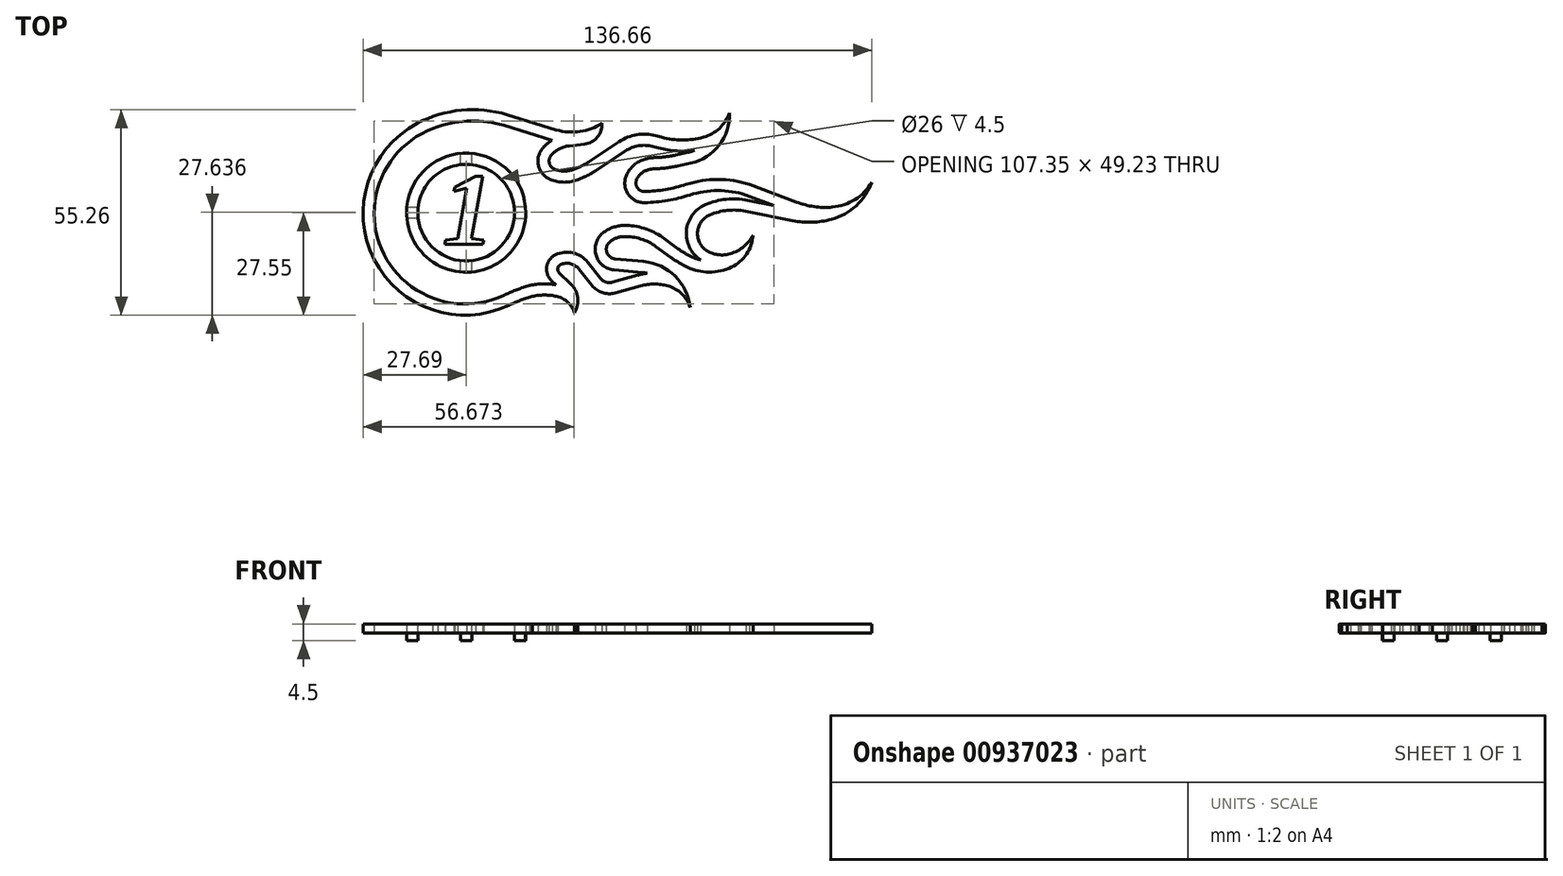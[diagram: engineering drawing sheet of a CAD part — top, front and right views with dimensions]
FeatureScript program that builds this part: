
annotation { "Feature Type Name" : "Feature", "Feature Type Description" : "" }
export const myFeature = defineFeature(function(context is Context, id is Id, definition is map)
    precondition{}
    {
        {
            var Q0;
            Q0=qCreatedBy(makeId("Top.planeOp"),FACE);
            cPlane(context, id + "F0", {"entities" : qUnion([Q0]), "cplaneType" : CPlaneType.OFFSET, "offset" : 2 * mm, "width" : 150 * mm, "height" : 150 * mm});
        }
        {
            var Q0;
            Q0=qCreatedBy(id+"F0.planeOp",FACE);
            var sketch = newSketch(context, id + "F1", { "sketchPlane" : qUnion([Q0])});
            skArc(sketch, "E0", {"start": v(-15.8, 20.8) * mm, "mid": v(-9.44, 20.3) * mm, "end": v(-3.49, 22.58) * mm});
            skLineSegment(sketch, "E1", {"start": v(-29, 24.82) * mm, "end": v(-15.8, 20.8) * mm});
            skArc(sketch, "E2", {"start": v(-53.14, 22.5) * mm, "mid": v(-64.76, -14.01) * mm, "end": v(-28.48, -26.36) * mm});
            skArc(sketch, "E3", {"start": v(-29, 24.82) * mm, "mid": v(-41.3, 26.06) * mm, "end": v(-53.14, 22.5) * mm});
            skArc(sketch, "E4", {"start": v(-8.25, 16.94) * mm, "mid": v(-4.75, 18.81) * mm, "end": v(-3.49, 22.58) * mm});
            skArc(sketch, "E5", {"start": v(-10.87, -28.44) * mm, "mid": v(-12.7, -25.58) * mm, "end": v(-15.7, -24) * mm});
            skArc(sketch, "E6", {"start": v(-15.7, -24) * mm, "mid": v(-18.94, -23.64) * mm, "end": v(-22.18, -24) * mm});
            skArc(sketch, "E7", {"start": v(-22.18, -24) * mm, "mid": v(-25.39, -25.04) * mm, "end": v(-28.48, -26.36) * mm});
            skArc(sketch, "E8", {"start": v(-10.87, -28.44) * mm, "mid": v(-10.04, -24.35) * mm, "end": v(-11.9, -20.62) * mm});
            skArc(sketch, "E9", {"start": v(-14.69, -15.51) * mm, "mid": v(-15.4, -16.45) * mm, "end": v(-15.02, -17.57) * mm});
            skLineSegment(sketch, "E10", {"start": v(-11.9, -20.62) * mm, "end": v(-15.02, -17.57) * mm});
            skArc(sketch, "E11", {"start": v(-9.7, -16.65) * mm, "mid": v(-12, -15.2) * mm, "end": v(-14.69, -15.51) * mm});
            skLineSegment(sketch, "E12", {"start": v(-9.7, -16.65) * mm, "end": v(-6.22, -21.05) * mm});
            skArc(sketch, "E13", {"start": v(-6.22, -21.05) * mm, "mid": v(-3.42, -23) * mm, "end": v(0, -23.09) * mm});
            skLineSegment(sketch, "E14", {"start": v(-8.25, 16.94) * mm, "end": v(-12.34, 16.47) * mm});
            skArc(sketch, "E15", {"start": v(-12.34, 16.47) * mm, "mid": v(-14.96, 15.66) * mm, "end": v(-17.12, 13.97) * mm});
            skArc(sketch, "E16", {"start": v(-17.12, 13.97) * mm, "mid": v(-17.66, 11.88) * mm, "end": v(-16.27, 10.22) * mm});
            skArc(sketch, "E17", {"start": v(-16.27, 10.22) * mm, "mid": v(-13.63, 9.69) * mm, "end": v(-10.98, 10.22) * mm});
            skLineSegment(sketch, "E18", {"start": v(-10.98, 10.22) * mm, "end": v(-9.42, 10.88) * mm});
            skLineSegment(sketch, "E19", {"start": v(1.1, 17.58) * mm, "end": v(-6.91, 12.23) * mm});
            skArc(sketch, "E20.filletArc", {"start": v(-9.42, 10.88) * mm, "mid": v(-8.13, 11.5) * mm, "end": v(-6.91, 12.23) * mm});
            skArc(sketch, "E21", {"start": v(10.9, 19.2) * mm, "mid": v(5.82, 19.45) * mm, "end": v(1.1, 17.58) * mm});
            skLineSegment(sketch, "E22", {"start": v(10.9, 19.2) * mm, "end": v(12.5, 18.78) * mm});
            skArc(sketch, "E23", {"start": v(12.5, 18.78) * mm, "mid": v(18.13, 18.04) * mm, "end": v(23.76, 18.78) * mm});
            skArc(sketch, "E24", {"start": v(23.76, 18.78) * mm, "mid": v(28.06, 21.17) * mm, "end": v(30.72, 25.31) * mm});
            skArc(sketch, "E25", {"start": v(20.3, 11.8) * mm, "mid": v(27.98, 16.65) * mm, "end": v(30.72, 25.31) * mm});
            skLineSegment(sketch, "E26", {"start": v(20.3, 11.8) * mm, "end": v(16.86, 11.06) * mm});
            skArc(sketch, "E27", {"start": v(10.82, 10.32) * mm, "mid": v(13.86, 10.55) * mm, "end": v(16.86, 11.06) * mm});
            skArc(sketch, "E28", {"start": v(10.82, 10.32) * mm, "mid": v(9.84, 10.23) * mm, "end": v(8.87, 10.03) * mm});
            skArc(sketch, "E29", {"start": v(8.87, 10.03) * mm, "mid": v(7.03, 9.04) * mm, "end": v(5.8, 7.34) * mm});
            skArc(sketch, "E30", {"start": v(5.8, 7.34) * mm, "mid": v(6.02, 5.16) * mm, "end": v(7.97, 4.17) * mm});
            skArc(sketch, "E31", {"start": v(19.12, 6.1) * mm, "mid": v(13.61, 4.74) * mm, "end": v(7.97, 4.17) * mm});
            skArc(sketch, "E32", {"start": v(36.14, 6.1) * mm, "mid": v(27.63, 7.44) * mm, "end": v(19.12, 6.1) * mm});
            skLineSegment(sketch, "E33", {"start": v(0, -23.09) * mm, "end": v(6.9, -21.19) * mm});
            skArc(sketch, "E34", {"start": v(14.19, -21.19) * mm, "mid": v(10.54, -20.7) * mm, "end": v(6.9, -21.19) * mm});
            skArc(sketch, "E35", {"start": v(20.17, -27.02) * mm, "mid": v(17.93, -23.33) * mm, "end": v(14.19, -21.19) * mm});
            skArc(sketch, "E36", {"start": v(20.17, -27.02) * mm, "mid": v(16.15, -18.57) * mm, "end": v(7.68, -14.62) * mm});
            skLineSegment(sketch, "E37", {"start": v(7.68, -14.62) * mm, "end": v(0, -13.91) * mm});
            skArc(sketch, "E38", {"start": v(-1.39, -9.32) * mm, "mid": v(-2.24, -12.08) * mm, "end": v(0, -13.91) * mm});
            skArc(sketch, "E39", {"start": v(2.46, -7.92) * mm, "mid": v(0.42, -8.3) * mm, "end": v(-1.39, -9.32) * mm});
            skArc(sketch, "E40", {"start": v(10.98, -10.59) * mm, "mid": v(6.94, -8.56) * mm, "end": v(2.46, -7.92) * mm});
            skLineSegment(sketch, "E41", {"start": v(10.98, -10.59) * mm, "end": v(15.06, -13.54) * mm});
            skArc(sketch, "E42", {"start": v(15.06, -13.54) * mm, "mid": v(17.16, -14.93) * mm, "end": v(19.37, -16.1) * mm});
            skArc(sketch, "E43", {"start": v(19.37, -16.1) * mm, "mid": v(25.34, -17.46) * mm, "end": v(31.3, -16.1) * mm});
            skArc(sketch, "E44", {"start": v(31.3, -16.1) * mm, "mid": v(35.34, -12.64) * mm, "end": v(37.05, -7.6) * mm});
            skArc(sketch, "E45", {"start": v(30.4, -12.7) * mm, "mid": v(34.29, -10.88) * mm, "end": v(37.05, -7.6) * mm});
            skArc(sketch, "E46", {"start": v(24.84, -11.81) * mm, "mid": v(27.53, -12.78) * mm, "end": v(30.4, -12.7) * mm});
            skArc(sketch, "E47", {"start": v(25.48, -2.1) * mm, "mid": v(22.17, -6.76) * mm, "end": v(24.84, -11.81) * mm});
            skArc(sketch, "E48", {"start": v(35.02, -1.1) * mm, "mid": v(30.17, -0.88) * mm, "end": v(25.48, -2.1) * mm});
            skLineSegment(sketch, "E49", {"start": v(35.02, -1.1) * mm, "end": v(47.7, -3.63) * mm});
            skArc(sketch, "E50", {"start": v(47.7, -3.63) * mm, "mid": v(52.94, -4.06) * mm, "end": v(58.13, -3.3) * mm});
            skArc(sketch, "E51", {"start": v(58.13, -3.3) * mm, "mid": v(64.79, 0.34) * mm, "end": v(68.97, 6.67) * mm});
            skArc(sketch, "E52", {"start": v(58.36, 0) * mm, "mid": v(64.48, 2.05) * mm, "end": v(68.97, 6.67) * mm});
            skArc(sketch, "E53", {"start": v(48.76, 1.34) * mm, "mid": v(53.49, 0.13) * mm, "end": v(58.36, 0) * mm});
            skLineSegment(sketch, "E54", {"start": v(36.14, 6.1) * mm, "end": v(48.76, 1.34) * mm});
            skArc(sketch, "E55.0", {"start": v(-29.87, 21.95) * mm, "mid": v(-38.73, 23.2) * mm, "end": v(-47.54, 21.67) * mm});
            skArc(sketch, "E56", {"start": v(-48.94, 21.12) * mm, "mid": v(-62.73, -11.25) * mm, "end": v(-29.8, -23.67) * mm});
            skLineSegment(sketch, "E57", {"start": v(-48.94, 21.12) * mm, "end": v(-47.54, 21.67) * mm});
            skLineSegment(sketch, "E58.0", {"start": v(-29.87, 21.95) * mm, "end": v(-16.92, 18) * mm});
            skArc(sketch, "E59.0", {"start": v(-12.68, 19.45) * mm, "mid": v(-12.7, 19.44) * mm, "end": v(-12.72, 19.44) * mm});
            skLineSegment(sketch, "E60", {"start": v(-16.92, 18) * mm, "end": v(-16.92, 18) * mm});
            skArc(sketch, "E61", {"start": v(-16.92, 18) * mm, "mid": v(-18.2, 17.08) * mm, "end": v(-19.34, 15.99) * mm});
            skArc(sketch, "E62.0", {"start": v(-19.37, 15.96) * mm, "mid": v(-20.58, 11.21) * mm, "end": v(-17.43, 7.46) * mm});
            skArc(sketch, "E63.0", {"start": v(-17.43, 7.46) * mm, "mid": v(-13.63, 6.69) * mm, "end": v(-9.82, 7.46) * mm});
            skLineSegment(sketch, "E64.0", {"start": v(-9.82, 7.46) * mm, "end": v(-8.25, 8.12) * mm});
            skArc(sketch, "E65.0", {"start": v(-8.25, 8.12) * mm, "mid": v(-6.71, 8.86) * mm, "end": v(-5.25, 9.74) * mm});
            skLineSegment(sketch, "E66.0", {"start": v(2.76, 15.09) * mm, "end": v(-5.25, 9.74) * mm});
            skArc(sketch, "E67.0", {"start": v(10.13, 16.3) * mm, "mid": v(6.31, 16.5) * mm, "end": v(2.76, 15.09) * mm});
            skLineSegment(sketch, "E68.0", {"start": v(10.13, 16.3) * mm, "end": v(11.74, 15.88) * mm});
            skArc(sketch, "E69.0", {"start": v(11.74, 15.88) * mm, "mid": v(16.51, 15.1) * mm, "end": v(21.35, 15.25) * mm});
            skLineSegment(sketch, "E70.0", {"start": v(19.3, 14.65) * mm, "end": v(16.22, 13.99) * mm});
            skArc(sketch, "E71.0", {"start": v(19.66, 14.73) * mm, "mid": v(20.52, 14.95) * mm, "end": v(21.35, 15.25) * mm});
            skArc(sketch, "E72.0", {"start": v(10.73, 13.32) * mm, "mid": v(13.5, 13.53) * mm, "end": v(16.22, 13.99) * mm});
            skArc(sketch, "E73.0", {"start": v(10.73, 13.32) * mm, "mid": v(9.4, 13.2) * mm, "end": v(8.08, 12.92) * mm});
            skArc(sketch, "E74.0", {"start": v(8.08, 12.92) * mm, "mid": v(5.05, 11.3) * mm, "end": v(3.04, 8.52) * mm});
            skArc(sketch, "E75.0", {"start": v(3.04, 8.52) * mm, "mid": v(3.54, 3.47) * mm, "end": v(8.07, 1.17) * mm});
            skArc(sketch, "E76.0", {"start": v(20.04, 3.25) * mm, "mid": v(14.12, 1.79) * mm, "end": v(8.07, 1.17) * mm});
            skLineSegment(sketch, "E77.0", {"start": v(35.6, 1.84) * mm, "end": v(42.66, 0.43) * mm});
            skArc(sketch, "E78.0", {"start": v(35.6, 1.84) * mm, "mid": v(29.87, 2.1) * mm, "end": v(24.3, 0.67) * mm});
            skArc(sketch, "E79.0", {"start": v(24.3, 0.67) * mm, "mid": v(19.19, -6.38) * mm, "end": v(23, -14.2) * mm});
            skArc(sketch, "E80.0", {"start": v(20.66, -13.4) * mm, "mid": v(21.81, -13.87) * mm, "end": v(23, -14.2) * mm});
            skArc(sketch, "E81.0", {"start": v(16.82, -11.12) * mm, "mid": v(18.69, -12.35) * mm, "end": v(20.66, -13.4) * mm});
            skLineSegment(sketch, "E82.0", {"start": v(12.74, -8.16) * mm, "end": v(16.82, -11.12) * mm});
            skArc(sketch, "E83.0", {"start": v(12.74, -8.16) * mm, "mid": v(7.83, -5.7) * mm, "end": v(2.4, -4.92) * mm});
            skArc(sketch, "E84.0", {"start": v(2.4, -4.92) * mm, "mid": v(-0.61, -5.48) * mm, "end": v(-3.28, -7) * mm});
            skArc(sketch, "E85.0", {"start": v(-3.28, -7) * mm, "mid": v(-5.11, -12.95) * mm, "end": v(-0.28, -16.9) * mm});
            skLineSegment(sketch, "E86.0", {"start": v(7.4, -17.6) * mm, "end": v(-0.28, -16.9) * mm});
            skLineSegment(sketch, "E87.0", {"start": v(-0.8, -20.2) * mm, "end": v(6.1, -18.3) * mm});
            skArc(sketch, "E88", {"start": v(8.67, -17.8) * mm, "mid": v(8.04, -17.68) * mm, "end": v(7.4, -17.6) * mm});
            skArc(sketch, "E89", {"start": v(8.67, -17.8) * mm, "mid": v(7.38, -18) * mm, "end": v(6.1, -18.3) * mm});
            skArc(sketch, "E90.0", {"start": v(-3.87, -19.2) * mm, "mid": v(-2.48, -20.16) * mm, "end": v(-0.8, -20.2) * mm});
            skLineSegment(sketch, "E91.0", {"start": v(-7.35, -14.8) * mm, "end": v(-3.87, -19.2) * mm});
            skArc(sketch, "E92.0", {"start": v(-7.35, -14.8) * mm, "mid": v(-11.32, -12.28) * mm, "end": v(-16, -12.81) * mm});
            skArc(sketch, "E93.0", {"start": v(-16, -12.81) * mm, "mid": v(-18.35, -15.97) * mm, "end": v(-17.12, -19.72) * mm});
            skLineSegment(sketch, "E94.0", {"start": v(-15.9, -20.9) * mm, "end": v(-17.12, -19.72) * mm});
            skArc(sketch, "E95.0", {"start": v(-15.9, -20.9) * mm, "mid": v(-19.4, -20.64) * mm, "end": v(-22.86, -21.08) * mm});
            skArc(sketch, "E96.0", {"start": v(-22.98, -21.11) * mm, "mid": v(-26.29, -22.18) * mm, "end": v(-29.49, -23.52) * mm});
            skLineSegment(sketch, "E97", {"start": v(-22.98, -21.11) * mm, "end": v(-22.86, -21.08) * mm});
            skLineSegment(sketch, "E98", {"start": v(19.3, 14.65) * mm, "end": v(19.66, 14.73) * mm});
            skLineSegment(sketch, "E99", {"start": v(-19.37, 15.96) * mm, "end": v(-19.34, 15.99) * mm});
            skArc(sketch, "E100", {"start": v(35.15, 3.27) * mm, "mid": v(27.6, 4.44) * mm, "end": v(20.04, 3.25) * mm});
            skLineSegment(sketch, "E101", {"start": v(35.15, 3.27) * mm, "end": v(42.66, 0.43) * mm});
            skLineSegment(sketch, "E102", {"start": v(-29.8, -23.67) * mm, "end": v(-29.49, -23.52) * mm});
            skSolve(sketch);
        }
        {
            var Q0;
            Q0 = qSketchRegion(id + "F1", true);
            extrude(context, id + "F2", {"entities" : qUnion([Q0]), "depth" : 2.5 * mm, "offsetDistance" : 25 * mm});
        }
        {
            var Q0;
            Q0=qCreatedBy(makeId("Top.planeOp"),FACE);
            var sketch = newSketch(context, id + "F3", { "sketchPlane" : qUnion([Q0])});
            skCircle(sketch, "E103", {"center": v(-40, -1.5) * mm, "radius": 16 * mm});
            skCircle(sketch, "E104", {"center": v(-40, -1.5) * mm, "radius": 13 * mm});
            skSolve(sketch);
        }
        {
            var Q0;
            Q0 = qSketchRegion(id + "F3", true);
            extrude(context, id + "F4", {"entities" : qUnion([Q0]), "operationType" : NewBodyOperationType.ADD, "depth" : 4.5 * mm, "offsetDistance" : 25 * mm});
        }
        {
            var Q0;
            Q0=qCreatedBy(id+"F0.planeOp",FACE);
            var sketch = newSketch(context, id + "F5", { "sketchPlane" : qUnion([Q0])});
            skText(sketch, "E105", { "text": "1", "fontName": "Tinos-BoldItalic.ttf"});
            const initialGuessF5  = {"E105": [-0.0464, -0.01, 1, 0, 0.02]};
            skSetInitialGuess(sketch, initialGuessF5);
            skSolve(sketch);
        }
        {
            var Q0;
            Q0 = qSketchRegion(id + "F5", true);
            extrude(context, id + "F6", {"entities" : qUnion([Q0]), "depth" : 2.5 * mm, "offsetDistance" : 25 * mm});
        }
        {
            var Q0;
            Q0=qCreatedBy(makeId("Top.planeOp"),FACE);
            var sketch = newSketch(context, id + "F7", { "sketchPlane" : qUnion([Q0])});
            skArc(sketch, "E106", {"start": v(-38.5, -17.43) * mm, "mid": v(-28.69, -12.81) * mm, "end": v(-24.07, -3) * mm});
            skArc(sketch, "E107", {"start": v(-38.5, -14.41) * mm, "mid": v(-30.8, -10.7) * mm, "end": v(-27.09, -3) * mm});
            skArc(sketch, "E108", {"start": v(-27.09, 0) * mm, "mid": v(-30.8, 7.7) * mm, "end": v(-38.5, 11.41) * mm});
            skArc(sketch, "E109", {"start": v(-24.07, 0) * mm, "mid": v(-28.69, 9.81) * mm, "end": v(-38.5, 14.43) * mm});
            skArc(sketch, "E110", {"start": v(-52.91, -3) * mm, "mid": v(-49.2, -10.7) * mm, "end": v(-41.5, -14.41) * mm});
            skArc(sketch, "E111", {"start": v(-55.93, -3) * mm, "mid": v(-51.31, -12.81) * mm, "end": v(-41.5, -17.43) * mm});
            skArc(sketch, "E112", {"start": v(-41.5, 14.43) * mm, "mid": v(-51.31, 9.81) * mm, "end": v(-55.93, 0) * mm});
            skArc(sketch, "E113", {"start": v(-41.5, 11.41) * mm, "mid": v(-49.19, 7.7) * mm, "end": v(-52.91, 0.02) * mm});
            skLineSegment(sketch, "E114", {"start": v(-41.5, -17.43) * mm, "end": v(-41.5, -14.41) * mm});
            skLineSegment(sketch, "E115", {"start": v(-38.5, -17.43) * mm, "end": v(-38.5, -14.41) * mm});
            skLineSegment(sketch, "E116", {"start": v(-27.09, -3) * mm, "end": v(-24.07, -3) * mm});
            skLineSegment(sketch, "E117", {"start": v(-24.07, 0) * mm, "end": v(-27.09, 0) * mm});
            skLineSegment(sketch, "E118", {"start": v(-38.5, 11.41) * mm, "end": v(-38.5, 14.43) * mm});
            skLineSegment(sketch, "E119", {"start": v(-41.5, 11.41) * mm, "end": v(-41.5, 14.43) * mm});
            skLineSegment(sketch, "E120", {"start": v(-52.91, -3) * mm, "end": v(-55.93, -3) * mm});
            skLineSegment(sketch, "E121", {"start": v(-55.93, 0) * mm, "end": v(-52.91, 0.02) * mm});
            skSolve(sketch);
        }
        {
            var Q0;
            Q0 = qSketchRegion(id + "F7", true);
            extrude(context, id + "F8", {"entities" : qUnion([Q0]), "operationType" : NewBodyOperationType.REMOVE, "depth" : 2 * mm, "offsetDistance" : 25 * mm});
        }
    });
